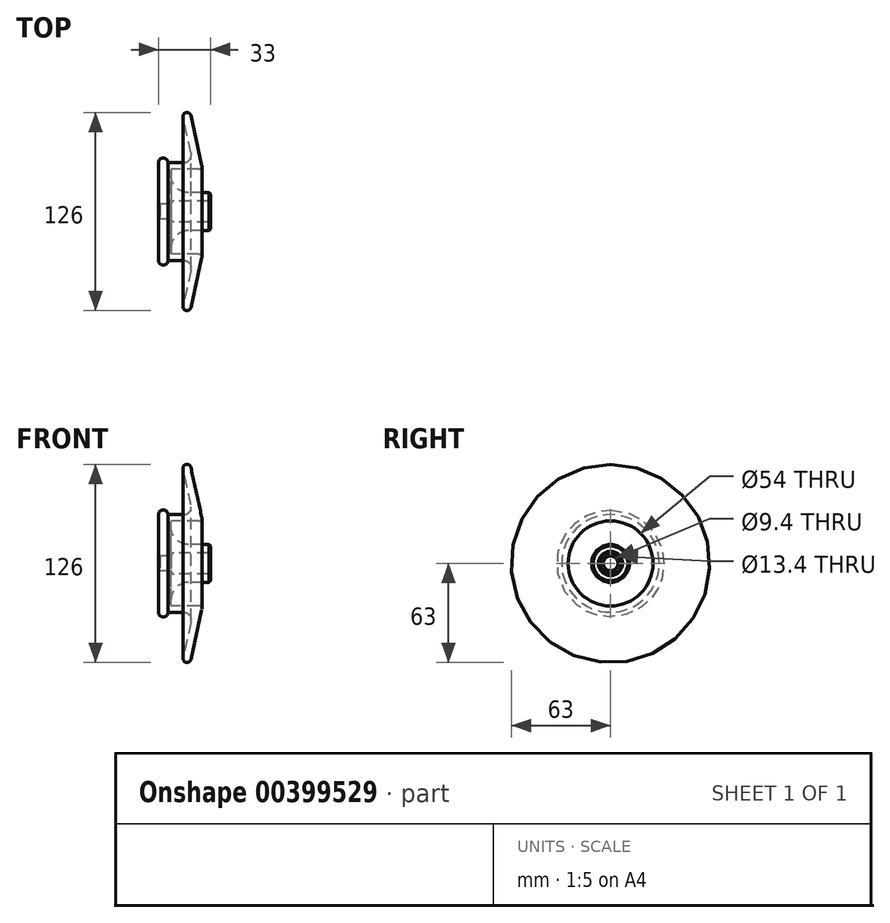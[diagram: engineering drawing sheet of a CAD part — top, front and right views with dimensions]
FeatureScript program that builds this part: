
annotation { "Feature Type Name" : "Feature", "Feature Type Description" : "" }
export const myFeature = defineFeature(function(context is Context, id is Id, definition is map)
    precondition{}
    {
        {
            var Q0;
            Q0=qCreatedBy(makeId("Front.planeOp"),FACE);
            var sketch = newSketch(context, id + "F0", { "sketchPlane" : qUnion([Q0])});
            skLineSegment(sketch, "E0", {"start": v(-13.52, 0) * mm, "end": v(15.8, 0) * mm, "construction": true});
            skLineSegment(sketch, "E1", {"start": v(0, 4.7) * mm, "end": v(0, 31) * mm});
            skLineSegment(sketch, "E2", {"start": v(22, 31) * mm, "end": v(15, 63) * mm});
            skLineSegment(sketch, "E3", {"start": v(15, 63) * mm, "end": v(20.12, 63) * mm});
            skLineSegment(sketch, "E4", {"start": v(28, 27) * mm, "end": v(8, 27) * mm});
            skLineSegment(sketch, "E5", {"start": v(8, 27) * mm, "end": v(8, 12) * mm});
            skLineSegment(sketch, "E6", {"start": v(8, 12) * mm, "end": v(33, 12) * mm});
            skLineSegment(sketch, "E7", {"start": v(33, 12) * mm, "end": v(33, 6.7) * mm});
            skLineSegment(sketch, "E8", {"start": v(33, 6.7) * mm, "end": v(8, 6.7) * mm});
            skLineSegment(sketch, "E9", {"start": v(8, 6.7) * mm, "end": v(8, 4.7) * mm});
            skLineSegment(sketch, "E10", {"start": v(8, 4.7) * mm, "end": v(0, 4.7) * mm});
            skArc(sketch, "E11", {"start": v(6, 31) * mm, "mid": v(3, 34) * mm, "end": v(0, 31) * mm});
            skLineSegment(sketch, "E12.trimOffspring", {"start": v(6, 31) * mm, "end": v(22, 31) * mm});
            skLineSegment(sketch, "E13", {"start": v(0, 31) * mm, "end": v(6, 31) * mm, "construction": true});
            skLineSegment(sketch, "E14", {"start": v(28, 27) * mm, "end": v(20.12, 63) * mm});
            skPoint(sketch, "E14.endSnap0", {"position": v(17.57, 63) * mm});
            skPoint(sketch, "E15.start.orphan", {"position": v(33, 31) * mm});
            skPoint(sketch, "E16.orphan", {"position": v(20.15, 63) * mm});
            skSolve(sketch);
        }
        {
            var Q0;
            Q0=makeQuery(id+"F0.imprint","IMPRINT",FACE,{"disambiguationData":[TD([[makeQuery(id+"F0.imprint","IMPRINT",EDGE,{"derivedFrom":sQuery(id+"F0.wireOp",EDGE,"E1")}),-1.0]])]});
            var Q1;
            Q1=sQuery(id+"F0.wireOp",EDGE,"E0");
            revolve(context, id + "F1", {"entities" : qUnion([Q0]), "axis" : qUnion([Q1]), "revolveType" : RevolveType.FULL});
        }
        {
            var Q0;
            Q0=makeQuery(id+"F1.opRevolve","SWEPT_EDGE",EDGE,{"disambiguationData":[OSD([sQuery(id+"F0.wireOp",EDGE,"E4"),sQuery(id+"F0.wireOp",EDGE,"E5")])]});
            fillet(context, id + "F2", {"entities" : qUnion([Q0]), "radius" : .5 * mm, "tangentPropagation" : true, "allowEdgeOverflow" : false});
        }
        {
            var Q0;
            Q0=makeQuery(id+"F1.opRevolve","SWEPT_EDGE",EDGE,{"disambiguationData":[OSD([sQuery(id+"F0.wireOp",EDGE,"E4"),sQuery(id+"F0.wireOp",EDGE,"E14")])]});
            fillet(context, id + "F3", {"entities" : qUnion([Q0]), "radius" : 2 * mm, "tangentPropagation" : true, "allowEdgeOverflow" : false});
        }
        {
            var Q0;
            Q0=makeQuery(id+"F1.opRevolve","SWEPT_FACE",FACE,{"disambiguationData":[OSD([sQuery(id+"F0.wireOp",EDGE,"E7")])]});
            chamfer(context, id + "F4", {"entities" : qUnion([Q0]), "width" : 1 * mm, "tangentPropagation" : true});
        }
        {
            var Q0;
            Q0=makeQuery(id+"F1.opRevolve","SWEPT_EDGE",EDGE,{"disambiguationData":[OSD([sQuery(id+"F0.wireOp",EDGE,"E5"),sQuery(id+"F0.wireOp",EDGE,"E6")])]});
            fillet(context, id + "F5", {"entities" : qUnion([Q0]), "radius" : 11 * mm, "tangentPropagation" : true, "allowEdgeOverflow" : false});
        }
        {
            var Q0;
            Q0=makeQuery(id+"F1.opRevolve","SWEPT_EDGE",EDGE,{"disambiguationData":[OSD([sQuery(id+"F0.wireOp",EDGE,"E8"),sQuery(id+"F0.wireOp",EDGE,"E9")])]});
            fillet(context, id + "F6", {"entities" : qUnion([Q0]), "radius" : 2 * mm, "tangentPropagation" : true, "allowEdgeOverflow" : false});
        }
        {
            var Q0;
            Q0=makeQuery(id+"F1.opRevolve","SWEPT_EDGE",EDGE,{"disambiguationData":[OSD([sQuery(id+"F0.wireOp",EDGE,"E1"),sQuery(id+"F0.wireOp",EDGE,"E10")])]});
            chamfer(context, id + "F7", {"entities" : qUnion([Q0]), "width" : 1 * mm, "tangentPropagation" : true});
        }
        {
            var Q0;
            Q0=makeQuery(id+"F1.opRevolve","SWEPT_EDGE",EDGE,{"disambiguationData":[OSD([sQuery(id+"F0.wireOp",EDGE,"E2"),sQuery(id+"F0.wireOp",EDGE,"E3")])]});
            var Q1;
            Q1=makeQuery(id+"F1.opRevolve","SWEPT_EDGE",EDGE,{"disambiguationData":[OSD([sQuery(id+"F0.wireOp",EDGE,"E3"),sQuery(id+"F0.wireOp",EDGE,"E14")])]});
            fillet(context, id + "F8", {"entities" : qUnion([Q0, Q1]), "radius" : 2.5 * mm, "tangentPropagation" : true, "allowEdgeOverflow" : false});
        }
        {
            var Q0;
            Q0=makeQuery(id+"F1.opRevolve","SWEPT_EDGE",EDGE,{"disambiguationData":[OSD([sQuery(id+"F0.wireOp",EDGE,"E2"),sQuery(id+"F0.wireOp",EDGE,"E12.trimOffspring")])]});
            fillet(context, id + "F9", {"entities" : qUnion([Q0]), "radius" : 5 * mm, "tangentPropagation" : true, "allowEdgeOverflow" : false});
        }
    });
